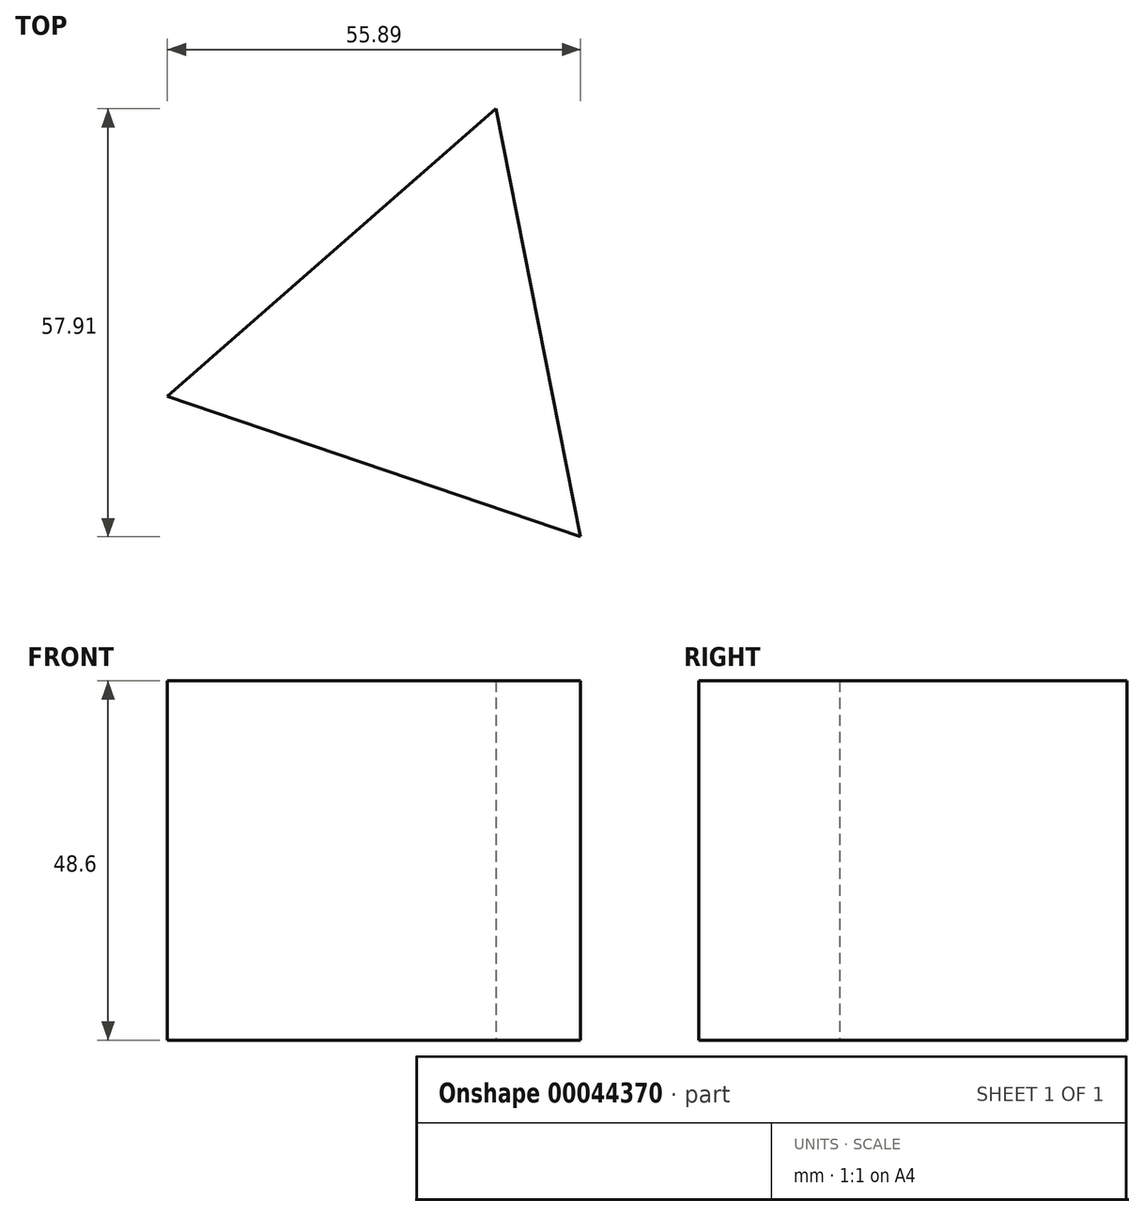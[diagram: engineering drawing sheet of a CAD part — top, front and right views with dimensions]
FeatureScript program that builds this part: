
annotation { "Feature Type Name" : "Feature", "Feature Type Description" : "" }
export const myFeature = defineFeature(function(context is Context, id is Id, definition is map)
    precondition{}
    {
        {
            var Q0;
            Q0=qCreatedBy(makeId("Top.planeOp"),FACE);
            var sketch = newSketch(context, id + "F0", { "sketchPlane" : qUnion([Q0])});
            skCircle(sketch, "E0.cCircle", {"center": v(-66.25, 24.33) * mm, "radius": 17.04 * mm, "construction": true});
            skLineSegment(sketch, "E0.0", {"start": v(-99.69, 17.7) * mm, "end": v(-55.27, 56.6) * mm});
            skLineSegment(sketch, "E0.1", {"start": v(-55.27, 56.6) * mm, "end": v(-43.8, -1.3) * mm});
            skLineSegment(sketch, "E0.2", {"start": v(-43.8, -1.3) * mm, "end": v(-99.69, 17.7) * mm});
            skPoint(sketch, "E0.0.midPoint", {"position": v(-77.48, 37.15) * mm});
            skSolve(sketch);
        }
        {
            var Q0;
            Q0=makeQuery(id+"F0.imprint","IMPRINT",FACE,{"disambiguationData":[TD([[makeQuery(id+"F0.imprint","IMPRINT",EDGE,{"derivedFrom":sQuery(id+"F0.wireOp",EDGE,"E0.0")}),-1.0]])]});
            extrude(context, id + "F1", {"entities" : qUnion([Q0]), "depth" : 48.6 * mm});
        }
    });
